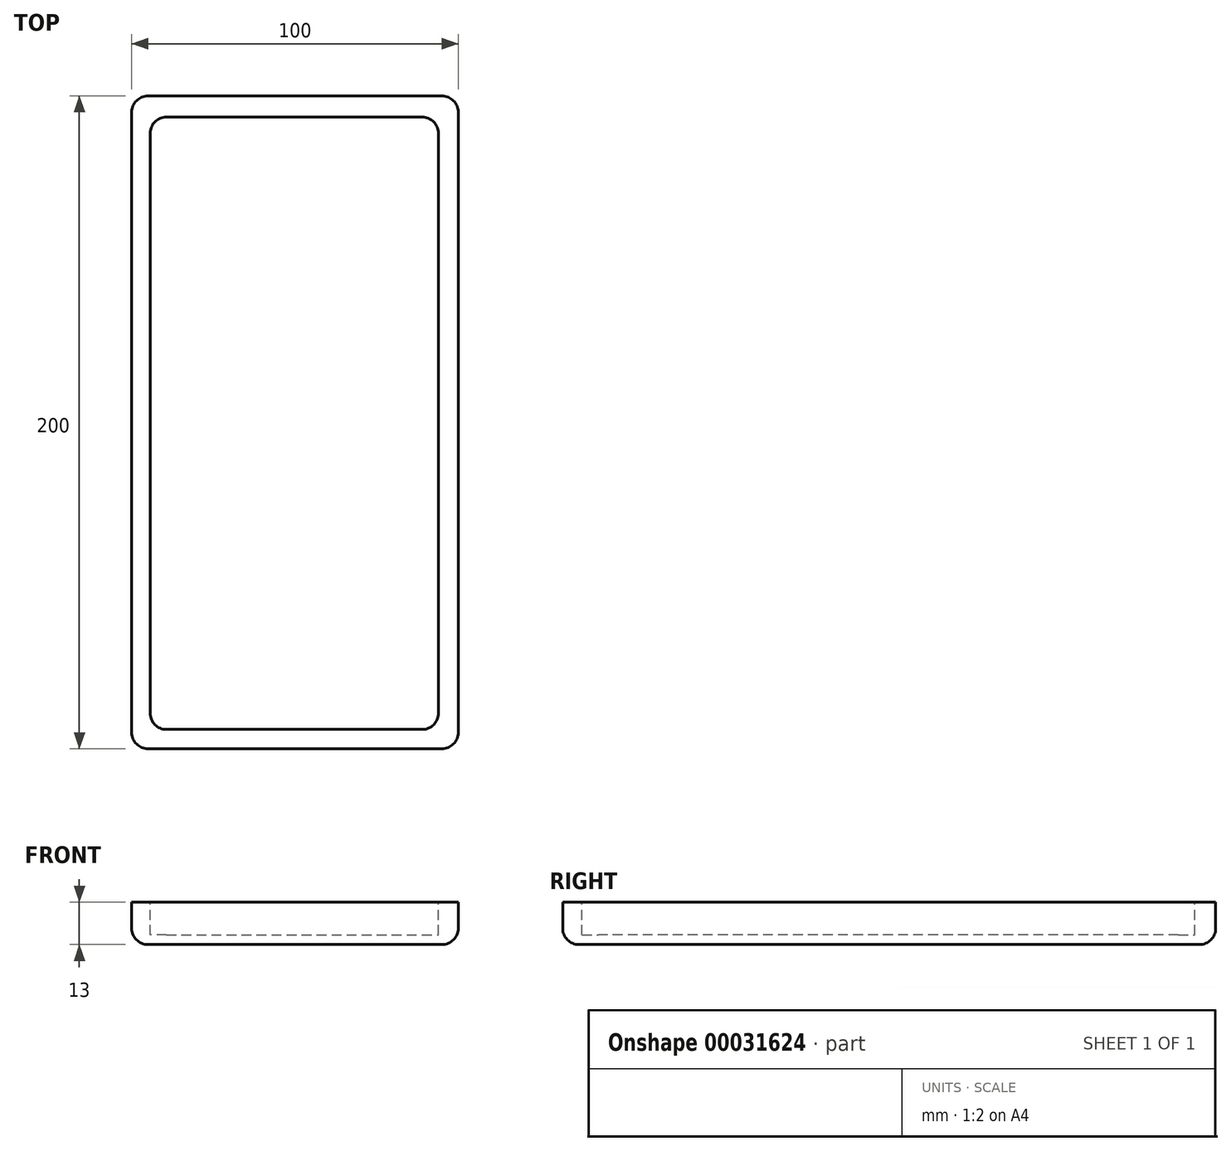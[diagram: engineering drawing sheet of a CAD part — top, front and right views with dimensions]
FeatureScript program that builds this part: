
annotation { "Feature Type Name" : "Feature", "Feature Type Description" : "" }
export const myFeature = defineFeature(function(context is Context, id is Id, definition is map)
    precondition{}
    {
        {
            var Q0;
            Q0=qCreatedBy(makeId("Top.planeOp"),FACE);
            var sketch = newSketch(context, id + "F0", { "sketchPlane" : qUnion([Q0])});
            skLineSegment(sketch, "E0.bottom", {"start": v(0, 0) * mm, "end": v(100, 0) * mm});
            skLineSegment(sketch, "E0.top", {"start": v(0, 200) * mm, "end": v(100, 200) * mm});
            skLineSegment(sketch, "E0.left", {"start": v(0, 0) * mm, "end": v(0, 200) * mm});
            skLineSegment(sketch, "E0.right", {"start": v(100, 0) * mm, "end": v(100, 200) * mm});
            skSolve(sketch);
        }
        {
            var Q0;
            Q0=makeQuery(id+"F0.imprint","IMPRINT",FACE,{"disambiguationData":[TD([[makeQuery(id+"F0.imprint","IMPRINT",EDGE,{"derivedFrom":sQuery(id+"F0.wireOp",EDGE,"E0.bottom")}),1.0]])]});
            extrude(context, id + "F1", {"entities" : qUnion([Q0]), "depth" : 13 * mm});
        }
        {
            var Q0;
            Q0=makeQuery(id+"F1.opExtrude","CAP_FACE",FACE,{"disambiguationData":[OSD([sQuery(id+"F0.wireOp",EDGE,"E0.bottom"),sQuery(id+"F0.wireOp",EDGE,"E0.top"),sQuery(id+"F0.wireOp",EDGE,"E0.left"),sQuery(id+"F0.wireOp",EDGE,"E0.right")])],"isStart":false});
            var sketch = newSketch(context, id + "F2", { "sketchPlane" : qUnion([Q0])});
            skSolve(sketch);
        }
        {
            var Q0;
            Q0=makeQuery(id+"F2.imprint","IMPRINT",FACE,{"disambiguationData":[TD([[makeQuery(id+"F2.imprint","IMPRINT",EDGE,{"derivedFrom":makeQuery(id+"F1.opExtrude","CAP_EDGE",EDGE,{"disambiguationData":[OSD([sQuery(id+"F0.wireOp",EDGE,"E0.bottom")])],"isStart":false})}),1.0]])]});
            var sketch = newSketch(context, id + "F3", { "sketchPlane" : qUnion([Q0])});
            skLineSegment(sketch, "E1.bottom", {"start": v(5.65, 193.53) * mm, "end": v(93.95, 193.53) * mm});
            skLineSegment(sketch, "E1.top", {"start": v(5.65, 5.91) * mm, "end": v(93.95, 5.91) * mm});
            skLineSegment(sketch, "E1.left", {"start": v(5.65, 193.53) * mm, "end": v(5.65, 5.91) * mm});
            skLineSegment(sketch, "E1.right", {"start": v(93.95, 193.53) * mm, "end": v(93.95, 5.91) * mm});
            skSolve(sketch);
        }
        {
            var Q0;
            Q0 = qSketchRegion(id + "F3", true);
            extrude(context, id + "F4", {"entities" : qUnion([Q0]), "operationType" : NewBodyOperationType.REMOVE, "oppositeDirection" : true, "depth" : 10 * mm});
        }
        {
            var Q0;
            Q0=makeQuery(id+"F1.opExtrude","SWEPT_EDGE",EDGE,{"disambiguationData":[OSD([sQuery(id+"F0.wireOp",EDGE,"E0.top"),sQuery(id+"F0.wireOp",EDGE,"E0.right")])]});
            fillet(context, id + "F5", {"entities" : qUnion([Q0]), "radius" : 5 * mm, "tangentPropagation" : true, "allowEdgeOverflow" : false});
        }
        {
            var Q0;
            Q0=makeQuery(id+"F1.opExtrude","SWEPT_EDGE",EDGE,{"disambiguationData":[OSD([sQuery(id+"F0.wireOp",EDGE,"E0.top"),sQuery(id+"F0.wireOp",EDGE,"E0.left")])]});
            fillet(context, id + "F6", {"entities" : qUnion([Q0]), "radius" : 5 * mm, "tangentPropagation" : true, "allowEdgeOverflow" : false});
        }
        {
            var Q0;
            Q0=makeQuery(id+"F1.opExtrude","SWEPT_EDGE",EDGE,{"disambiguationData":[OSD([sQuery(id+"F0.wireOp",EDGE,"E0.bottom"),sQuery(id+"F0.wireOp",EDGE,"E0.right")])]});
            fillet(context, id + "F7", {"entities" : qUnion([Q0]), "radius" : 5 * mm, "tangentPropagation" : true, "allowEdgeOverflow" : false});
        }
        {
            var Q0;
            Q0=makeQuery(id+"F1.opExtrude","SWEPT_EDGE",EDGE,{"disambiguationData":[OSD([sQuery(id+"F0.wireOp",EDGE,"E0.bottom"),sQuery(id+"F0.wireOp",EDGE,"E0.left")])]});
            fillet(context, id + "F8", {"entities" : qUnion([Q0]), "radius" : 5 * mm, "tangentPropagation" : true, "allowEdgeOverflow" : false});
        }
        {
            var Q0;
            Q0=makeQuery(id+"F4.boolean.opBoolean","COPY",EDGE,{"derivedFrom":makeQuery(id+"F4.opExtrude","SWEPT_EDGE",EDGE,{"disambiguationData":[OSD([sQuery(id+"F3.wireOp",EDGE,"E1.top"),sQuery(id+"F3.wireOp",EDGE,"E1.left")])]})});
            fillet(context, id + "F9", {"entities" : qUnion([Q0]), "radius" : 5 * mm, "tangentPropagation" : true, "allowEdgeOverflow" : false});
        }
        {
            var Q0;
            Q0=makeQuery(id+"F4.boolean.opBoolean","COPY",EDGE,{"derivedFrom":makeQuery(id+"F4.opExtrude","SWEPT_EDGE",EDGE,{"disambiguationData":[OSD([sQuery(id+"F3.wireOp",EDGE,"E1.bottom"),sQuery(id+"F3.wireOp",EDGE,"E1.left")])]})});
            fillet(context, id + "F10", {"entities" : qUnion([Q0]), "radius" : 5 * mm, "tangentPropagation" : true, "allowEdgeOverflow" : false});
        }
        {
            var Q0;
            Q0=makeQuery(id+"F4.boolean.opBoolean","COPY",EDGE,{"derivedFrom":makeQuery(id+"F4.opExtrude","SWEPT_EDGE",EDGE,{"disambiguationData":[OSD([sQuery(id+"F3.wireOp",EDGE,"E1.bottom"),sQuery(id+"F3.wireOp",EDGE,"E1.right")])]})});
            fillet(context, id + "F11", {"entities" : qUnion([Q0]), "radius" : 5 * mm, "tangentPropagation" : true, "allowEdgeOverflow" : false});
        }
        {
            var Q0;
            Q0=makeQuery(id+"F4.boolean.opBoolean","COPY",EDGE,{"derivedFrom":makeQuery(id+"F4.opExtrude","SWEPT_EDGE",EDGE,{"disambiguationData":[OSD([sQuery(id+"F3.wireOp",EDGE,"E1.top"),sQuery(id+"F3.wireOp",EDGE,"E1.right")])]})});
            fillet(context, id + "F12", {"entities" : qUnion([Q0]), "radius" : 5 * mm, "tangentPropagation" : true, "allowEdgeOverflow" : false});
        }
        {
            var Q0;
            Q0=makeQuery(id+"F1.opExtrude","CAP_EDGE",EDGE,{"disambiguationData":[OSD([sQuery(id+"F0.wireOp",EDGE,"E0.left")])],"isStart":true});
            fillet(context, id + "F13", {"entities" : qUnion([Q0]), "radius" : 5 * mm, "tangentPropagation" : true, "allowEdgeOverflow" : false});
        }
    });
